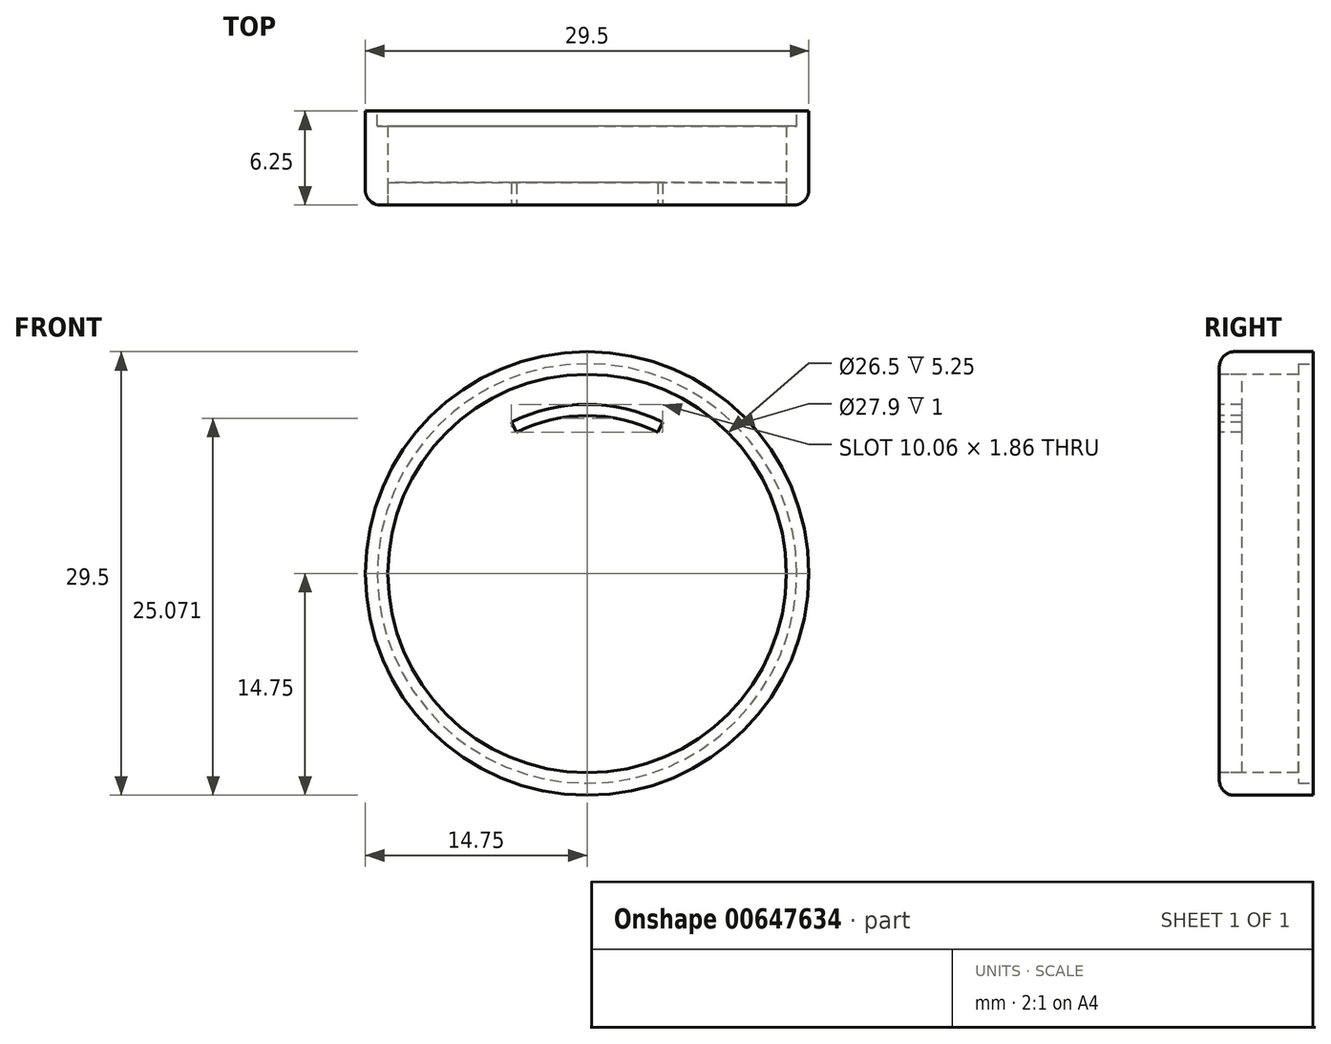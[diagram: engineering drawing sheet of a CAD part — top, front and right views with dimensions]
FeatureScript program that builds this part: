
annotation { "Feature Type Name" : "Feature", "Feature Type Description" : "" }
export const myFeature = defineFeature(function(context is Context, id is Id, definition is map)
    precondition{}
    {
        {
            var Q0;
            Q0=qCreatedBy(makeId("Front.planeOp"),FACE);
            var sketch = newSketch(context, id + "F0", { "sketchPlane" : qUnion([Q0])});
            skCircle(sketch, "E0", {"center": v(0, 0) * mm, "radius": 14.75 * mm});
            skCircle(sketch, "E1", {"center": v(0, 0) * mm, "radius": 13.25 * mm});
            skSolve(sketch);
        }
        {
            var Q0;
            Q0=makeQuery(id+"F0.imprint","IMPRINT",FACE,{"disambiguationData":[TD([[makeQuery(id+"F0.imprint","IMPRINT",EDGE,{"derivedFrom":sQuery(id+"F0.wireOp",EDGE,"E0")}),1.0]])]});
            extrude(context, id + "F1", {"entities" : qUnion([Q0]), "oppositeDirection" : true, "depth" : 6.25 * mm, "offsetDistance" : 25 * mm});
        }
        {
            var Q0;
            Q0=makeQuery(id+"F0.imprint","IMPRINT",FACE,{"disambiguationData":[TD([[makeQuery(id+"F0.imprint","IMPRINT",EDGE,{"derivedFrom":sQuery(id+"F0.wireOp",EDGE,"E1")}),1.0]])]});
            extrude(context, id + "F2", {"entities" : qUnion([Q0]), "oppositeDirection" : true, "depth" : 1.5 * mm, "offsetDistance" : 25 * mm});
        }
        {
            var Q0;
            Q0=makeQuery(id+"F1.opExtrude","CAP_FACE",FACE,{"disambiguationData":[OSD([sQuery(id+"F0.wireOp",EDGE,"E0"),sQuery(id+"F0.wireOp",EDGE,"E1")])],"isStart":false});
            var sketch = newSketch(context, id + "F3", { "sketchPlane" : qUnion([Q0])});
            skCircle(sketch, "E2", {"center": v(0, 0) * mm, "radius": 13.95 * mm});
            skCircle(sketch, "E3", {"center": v(0, 0) * mm, "radius": 13.25 * mm});
            skSolve(sketch);
        }
        {
            var Q0;
            Q0 = qSketchRegion(id + "F3", true);
            extrude(context, id + "F4", {"entities" : qUnion([Q0]), "operationType" : NewBodyOperationType.REMOVE, "oppositeDirection" : true, "depth" : 1 * mm, "offsetDistance" : 25 * mm});
        }
        {
            var Q0;
            Q0=makeQuery(id+"F1.opExtrude","CAP_EDGE",EDGE,{"disambiguationData":[OSD([sQuery(id+"F0.wireOp",EDGE,"E0")])],"isStart":true});
            fillet(context, id + "F5", {"entities" : qUnion([Q0]), "radius" : 1 * mm, "tangentPropagation" : true, "allowEdgeOverflow" : false});
        }
        {
            var Q0;
            Q0=makeQuery(id+"F0.imprint","IMPRINT",FACE,{"disambiguationData":[TD([[makeQuery(id+"F0.imprint","IMPRINT",EDGE,{"derivedFrom":sQuery(id+"F0.wireOp",EDGE,"E1")}),1.0]])]});
            var sketch = newSketch(context, id + "F6", { "sketchPlane" : qUnion([Q0])});
            skArc(sketch, "E4", {"start": v(5.03, 10.06) * mm, "mid": v(0, 11.25) * mm, "end": v(-5.03, 10.06) * mm});
            skArc(sketch, "E5", {"start": v(4.7, 9.4) * mm, "mid": v(0, 10.5) * mm, "end": v(-4.7, 9.4) * mm});
            skLineSegment(sketch, "E6", {"start": v(4.7, 9.4) * mm, "end": v(5.03, 10.06) * mm});
            skLineSegment(sketch, "E7.MirrorCS", {"start": v(-4.7, 9.4) * mm, "end": v(-5.03, 10.06) * mm});
            skSolve(sketch);
        }
        {
            var Q0;
            Q0 = qSketchRegion(id + "F6", true);
            extrude(context, id + "F7", {"entities" : qUnion([Q0]), "operationType" : NewBodyOperationType.REMOVE, "oppositeDirection" : true, "depth" : 1.5 * mm, "offsetDistance" : 25 * mm});
        }
    });
